# Revit family: Spannkralle 45
name_source: partatom
category: HLS-Bauteile
revit_build: Autodesk Revit 2017 (Build: 20190507_1515(x64)
units: mm (PartAtom-declared; Revit-internal decimal feet)

## family parameters
Basisbauteil = Fläche
Beim Laden mit Abzugskörper schneiden = Nein
Bemaßung runder Anschluss = Durchmesser verwenden
Gemeinsam genutzt = Ja
Raumberechnungspunkt = Nein
Teiletyp = Normal

## types (1)
- Spannkralle 45
    Artikelnummer = 08165071
    Breite = 80 mm  [stored 0.262467 ft]
    EAN = 4250928448002
    Fabrikat = MEFA
    Firma = MEFA Befestigungs- und Montagesysteme GmbH
    Gewicht = 0.34 kg
    Gewicht pro Bauteil = 0.34 kg
    Höhe = 83 mm
    Höhe Profil = 45 mm  [stored 0.147638 ft]
    Klemmdicke = 17 mm
    Kurztext1 = Spannkralle C-Profil 45
    Kurztext2 = Profilhöhe 45 mm Klemmdicke 17 mm
    Länge = 32 mm
    Material = Stahl
    Oberflaeche = galvanisch verzinkt
    Profil = C-Profil
    Profiltyp = 45
    Stärke = 6 mm  [stored 0.019685 ft]
    Vorgabe-Ansicht = 1219 mm
    max. zul. Last = 0.00 kip

note: [stored X ft] marks values corroborated as IEEE doubles in the binary element streams (Revit-internal decimal feet)
